# Revit family: 304_Cim788PRO(OT)-_
name_source: partatom
category: Pipe Accessories
units: mm (PartAtom-declared; Revit-internal decimal feet)

## family parameters
Always vertical = Yes
Cut with Voids When Loaded = No
Part Type = Valve - Breaks Into
Round Connector Dimension = Use Diameter
Shared = No
Work Plane-Based = No

## types (3) — shared parameters
CAT0 = Yes
DD3 = 40 mm  [stored 0.131234 ft]
DD4 = 23 mm
Description = PRE-SETTING BALANCING VALVE - VARIABLE ORIFICE - PN 25 -  PROPORTIONAL ACTUATOR 0-10 V
F = 45 mm  [stored 0.147638 ft]
HH3 = 3 mm  [stored 0.00984252 ft]
HH4 = 21 mm
HH5 = 58 mm  [stored 0.190289 ft]
HH6 = 4 mm  [stored 0.0131234 ft]
L2D_Min = 3048 mm
Manufacturer = Cimberio
QmdConnectorList = 301;D;302;D
R2 = 4 mm  [stored 0.0131234 ft]
URL = www.cimberio.it
magiPartTypeId = 304
magiProductFamilyId = Cim788PRO(OT)-*
zero-valued in all types: MC_Default_elevation

## per-type parameters (varying)
| type | AA1 | AA2 | BB1 | BB2 | CenSd_R1_6 | D | DD1 | DD2 | DL | DL__ve | HH1 | HH2 | L2D | LL1 | LL2 | LL2__ve | LL3 | LL3__ve | LL4 | R | R1 | W2D | WW1 |
| Cim788PRO(OT)-15 | 50 mm  [stored 0.164042 ft] | 36 mm | 39 mm | 36 mm | 8 mm  [stored 0.0262467 ft] | 15 mm | 18 mm | 25 mm  [stored 0.082021 ft] | 16 mm  [stored 0.0524934 ft] | -16 mm  [stored -0.0524934 ft] | 7 mm  [stored 0.0229659 ft] | 12 mm  [stored 0.0393701 ft] | 77 mm | 39 mm | 11 mm | -11 mm | 4 mm  [stored 0.0131234 ft] | -4 mm  [stored -0.0131234 ft] | 12 mm  [stored 0.0393701 ft] | 8 mm  [stored 0.0262467 ft] | 9 mm  [stored 0.0295276 ft] | 15 mm  [stored 0.0492126 ft] | 10 mm  [stored 0.0328084 ft] |
| Cim788PRO(OT)-25 | 51 mm | 40 mm  [stored 0.131234 ft] | 43 mm | 40 mm  [stored 0.131234 ft] | 13 mm | 25 mm | 20 mm  [stored 0.0656168 ft] | 28 mm | 21 mm | -21 mm | 11 mm | 21 mm | 87 mm | 44 mm | 12 mm  [stored 0.0393701 ft] | -12 mm | 1 mm  [stored 0.00328084 ft] | -1 mm  [stored -0.00328084 ft] | 14 mm  [stored 0.0459318 ft] | 13 mm | 15 mm  [stored 0.0492126 ft] | 25 mm  [stored 0.082021 ft] | 11 mm |
| Cim788PRO(OT)-20 | 51 mm | 37 mm | 40 mm  [stored 0.131234 ft] | 37 mm | 10 mm  [stored 0.0328084 ft] | 20 mm | 18 mm | 26 mm | 19 mm | -19 mm | 9 mm  [stored 0.0295276 ft] | 16 mm  [stored 0.0524934 ft] | 80 mm | 40 mm  [stored 0.131234 ft] | 11 mm | -11 mm | 1 mm  [stored 0.00328084 ft] | -1 mm  [stored -0.00328084 ft] | 13 mm | 10 mm  [stored 0.0328084 ft] | 12 mm  [stored 0.0393701 ft] | 20 mm  [stored 0.0656168 ft] | 10 mm  [stored 0.0328084 ft] |

note: column(s) folded — value = type name in every type: magiProductCode, magiProductId

note: [stored X ft] marks values corroborated as IEEE doubles in the binary element streams (Revit-internal decimal feet)

## geometry (parser evidence)
native form markers: Sweep x2
no freeform markers — native parametric forms only
